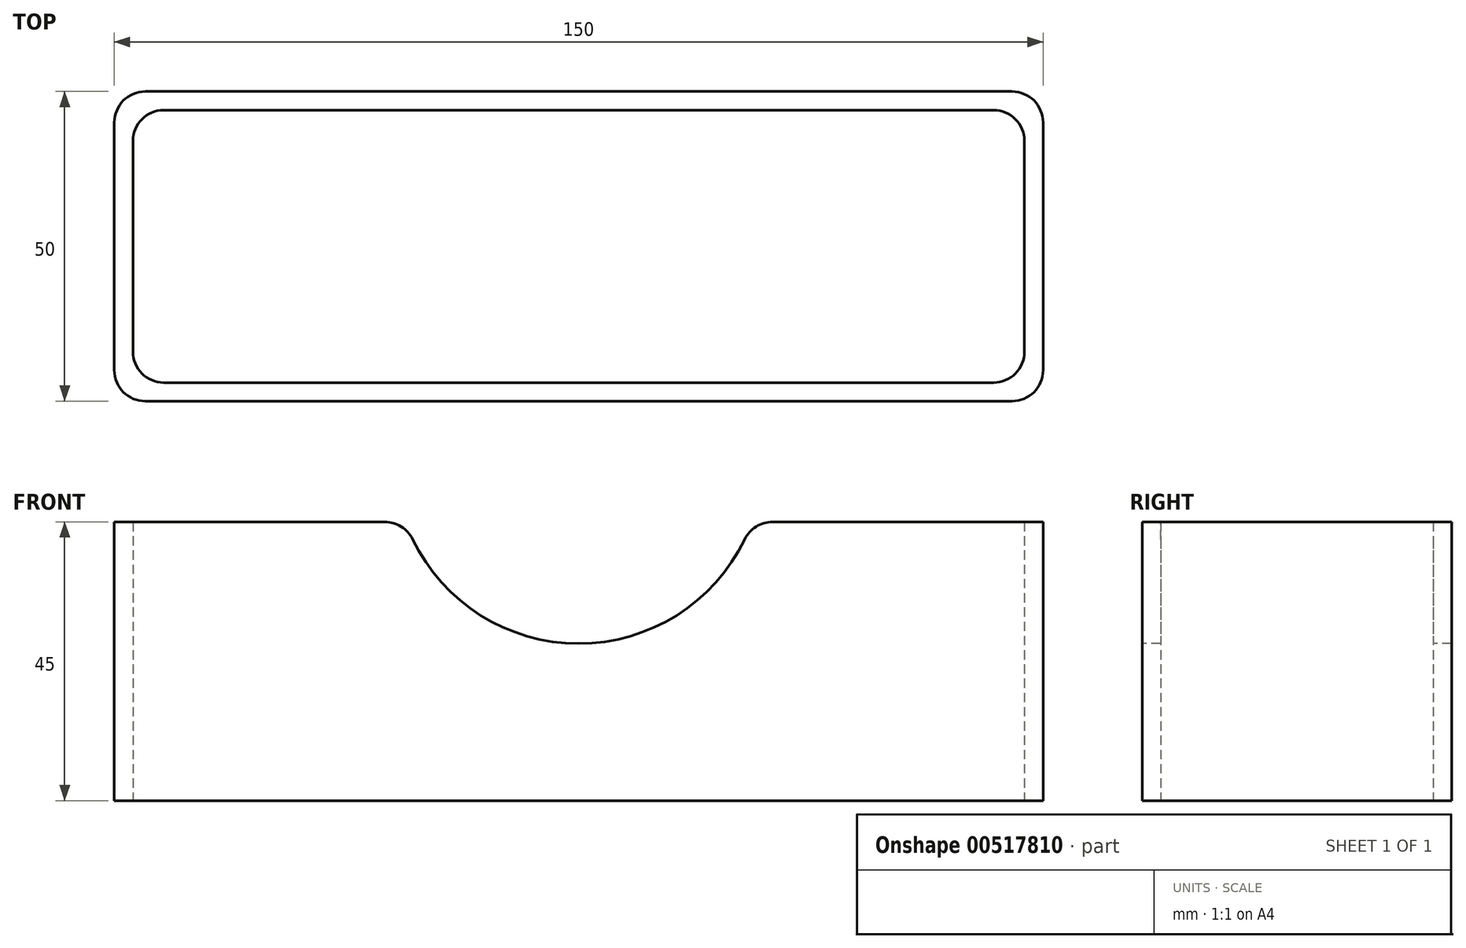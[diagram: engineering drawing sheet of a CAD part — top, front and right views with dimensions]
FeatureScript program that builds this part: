
annotation { "Feature Type Name" : "Feature", "Feature Type Description" : "" }
export const myFeature = defineFeature(function(context is Context, id is Id, definition is map)
    precondition{}
    {
        {
            var Q0;
            Q0=qCreatedBy(makeId("Top.planeOp"),FACE);
            var sketch = newSketch(context, id + "F0", { "sketchPlane" : qUnion([Q0])});
            skLineSegment(sketch, "E0.bottom", {"start": v(-75, 25) * mm, "end": v(75, 25) * mm});
            skLineSegment(sketch, "E0.top", {"start": v(-75, -25) * mm, "end": v(75, -25) * mm});
            skLineSegment(sketch, "E0.left", {"start": v(-75, 25) * mm, "end": v(-75, -25) * mm});
            skLineSegment(sketch, "E0.right", {"start": v(75, 25) * mm, "end": v(75, -25) * mm});
            skPoint(sketch, "E0.middle", {"position": v(0, 0) * mm});
            skLineSegment(sketch, "E1.bottom", {"start": v(72, 22) * mm, "end": v(-72, 22) * mm});
            skLineSegment(sketch, "E1.top", {"start": v(72, -22) * mm, "end": v(-72, -22) * mm});
            skLineSegment(sketch, "E1.left", {"start": v(72, 22) * mm, "end": v(72, -22) * mm});
            skLineSegment(sketch, "E1.right", {"start": v(-72, 22) * mm, "end": v(-72, -22) * mm});
            skSolve(sketch);
        }
        {
            var Q0;
            Q0=makeQuery(id+"F0.imprint","IMPRINT",FACE,{"disambiguationData":[TD([[makeQuery(id+"F0.imprint","IMPRINT",EDGE,{"derivedFrom":sQuery(id+"F0.wireOp",EDGE,"E0.bottom")}),-1.0]])]});
            extrude(context, id + "F1", {"entities" : qUnion([Q0]), "depth" : 45 * mm, "offsetDistance" : 25 * mm});
        }
        {
            var Q0;
            Q0=makeQuery(id+"F1.opExtrude","SWEPT_FACE",FACE,{"disambiguationData":[OSD([sQuery(id+"F0.wireOp",EDGE,"E0.top")])]});
            var sketch = newSketch(context, id + "F2", { "sketchPlane" : qUnion([Q0])});
            skArc(sketch, "E2", {"start": v(-26.81, 42.18) * mm, "mid": v(0, 25.35) * mm, "end": v(26.81, 42.18) * mm});
            skPoint(sketch, "E3.visualSharp", {"position": v(-28, 45) * mm});
            skArc(sketch, "E3.filletArc", {"start": v(-26.81, 42.18) * mm, "mid": v(-28.65, 44.24) * mm, "end": v(-31.31, 45) * mm});
            skPoint(sketch, "E4.visualSharp", {"position": v(28, 45) * mm});
            skArc(sketch, "E4.filletArc", {"start": v(31.31, 45) * mm, "mid": v(28.65, 44.24) * mm, "end": v(26.81, 42.18) * mm});
            skLineSegment(sketch, "E5", {"start": v(-31.31, 45) * mm, "end": v(31.31, 45) * mm});
            skSolve(sketch);
        }
        {
            var Q0;
            Q0=makeQuery(id+"F2.imprint","IMPRINT",FACE,{"disambiguationData":[TD([[makeQuery(id+"F2.imprint","IMPRINT",EDGE,{"derivedFrom":sQuery(id+"F2.wireOp",EDGE,"E2")}),1.0]])]});
            extrude(context, id + "F3", {"entities" : qUnion([Q0]), "operationType" : NewBodyOperationType.REMOVE, "oppositeDirection" : true, "depth" : 53.9 * mm, "offsetDistance" : 25 * mm});
        }
        {
            var Q0;
            Q0=makeQuery(id+"F1.opExtrude","SWEPT_EDGE",EDGE,{"disambiguationData":[OSD([sQuery(id+"F0.wireOp",EDGE,"E0.bottom"),sQuery(id+"F0.wireOp",EDGE,"E0.left")])]});
            var Q1;
            Q1=makeQuery(id+"F1.opExtrude","SWEPT_EDGE",EDGE,{"disambiguationData":[OSD([sQuery(id+"F0.wireOp",EDGE,"E0.top"),sQuery(id+"F0.wireOp",EDGE,"E0.left")])]});
            var Q2;
            Q2=makeQuery(id+"F1.opExtrude","SWEPT_EDGE",EDGE,{"disambiguationData":[OSD([sQuery(id+"F0.wireOp",EDGE,"E0.bottom"),sQuery(id+"F0.wireOp",EDGE,"E0.right")])]});
            var Q3;
            Q3=makeQuery(id+"F1.opExtrude","SWEPT_EDGE",EDGE,{"disambiguationData":[OSD([sQuery(id+"F0.wireOp",EDGE,"E0.top"),sQuery(id+"F0.wireOp",EDGE,"E0.right")])]});
            var Q4;
            Q4=makeQuery(id+"F1.opExtrude","SWEPT_EDGE",EDGE,{"disambiguationData":[OSD([sQuery(id+"F0.wireOp",EDGE,"E1.top"),sQuery(id+"F0.wireOp",EDGE,"E1.right")])]});
            var Q5;
            Q5=makeQuery(id+"F1.opExtrude","SWEPT_EDGE",EDGE,{"disambiguationData":[OSD([sQuery(id+"F0.wireOp",EDGE,"E1.top"),sQuery(id+"F0.wireOp",EDGE,"E1.left")])]});
            var Q6;
            Q6=makeQuery(id+"F1.opExtrude","SWEPT_EDGE",EDGE,{"disambiguationData":[OSD([sQuery(id+"F0.wireOp",EDGE,"E1.bottom"),sQuery(id+"F0.wireOp",EDGE,"E1.left")])]});
            var Q7;
            Q7=makeQuery(id+"F1.opExtrude","SWEPT_EDGE",EDGE,{"disambiguationData":[OSD([sQuery(id+"F0.wireOp",EDGE,"E1.bottom"),sQuery(id+"F0.wireOp",EDGE,"E1.right")])]});
            fillet(context, id + "F4", {"entities" : qUnion([Q0, Q1, Q2, Q3, Q4, Q5, Q6, Q7]), "radius" : 5 * mm, "tangentPropagation" : true, "allowEdgeOverflow" : false});
        }
    });
